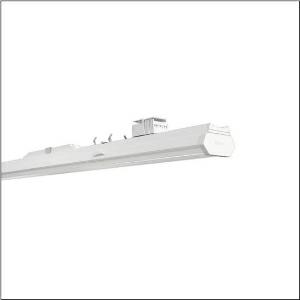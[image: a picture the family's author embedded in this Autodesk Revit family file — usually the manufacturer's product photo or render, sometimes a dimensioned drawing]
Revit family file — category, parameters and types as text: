
# Revit family: licross_r__21_performance_mo_52td167n485g_efc6
name_source: partatom
category: Lighting Fixtures
units: mm (PartAtom-declared; Revit-internal decimal feet)

## family parameters
Cut with Voids When Loaded = No
Host = Face
Light Source = No
Part Type = Normal
Room Calculation Point = No
Round Connector Dimension = Use Diameter
Shared = No

## types (1)
- Licross® 21 Performance MO (1 x LED, 8720 lm, 47.9 W, 4000K)
    Apparent Load = 48 VA
    CIE Flux Codes = 66 88 96 79 100
    Color Rendering = 80
    Color Temperature = 4000K
    Default Elevation = 1800 mm
    Description = Licross® 21 Performance MO, luminaire insert, of sheet steel, galvanised, coil coated, white, length: 1.500mm, width: 120mm, height: 123mm, LED rated luminous flux: 8.720lm, light colour: 840, control gear: ON/OFF, control gear: ECG, with plug, 3-pole, with phase selection, mains connection: 220..240V, AC, 50/60Hz, halogen-free wiring, primary light control with lens, of plastic, primary optical cover: cover, of PMMA, light emission: direct/indirect distribution, primary light characteristic: symmetric, protection rating (complete): IP54, insulation class (complete): insulation class I (protective earthing), certification: CE, ENEC, UKCA, protection symbol: D if used in an environment with non-conductive dust loads with corresponding accessories, impact resistance: IK06, permissible ambient temperature for indoor applications: -35..+45°C, corresponds to IFS (International Featured Standards) requirements for safety and quality in the food industry, reducing of maximum allowable ambient temperature of 5°C with ceiling mounting, LABS conformity tested according to VDMA 24364:2018-05, packaging unit: 1 piece
    Height = 114 mm
    Lamp = 1 x LED
    Lamp Light Flux = 8720 lm
    Lamp Power = 47.9 W
    Lamp count = 1
    Length = 1500 mm
    Luminous efficacy = 182 lm/W
    Manufacturer = Siteco
    ModVariant = No
    Model = 52TD167N485G
    Mounting Place = Ceiling
    Mounting Type = Pendant
    Number of Poles = 1
    OnlyDefault = Yes
    Power Factor = 1
    Product Name = Licross® 21 Performance MO
    Product group = luminaire insert
    ProductGroupID = 902
    Protection Class = Protection class I
    Protection Degree = IP 54
    RLX_Detail_Level = 1
    RlxData = <blob elided: 28213 chars, md5=53a6bd07>
    Socket = socket
    Standby Power = 0 W
    System Light Flux = 8720 lm
    System Power = 48 W
    Type Comments = Product without accessories
    Type Image = l_1256148.jpg
    URL = http://relux.com
    VarID = ---
    Voltage = 0 V
    Weight = 0.00 kg
    Width = 120 mm

## geometry (parser evidence)
native form markers: Blend x4, Sweep x12
no freeform markers — native parametric forms only
